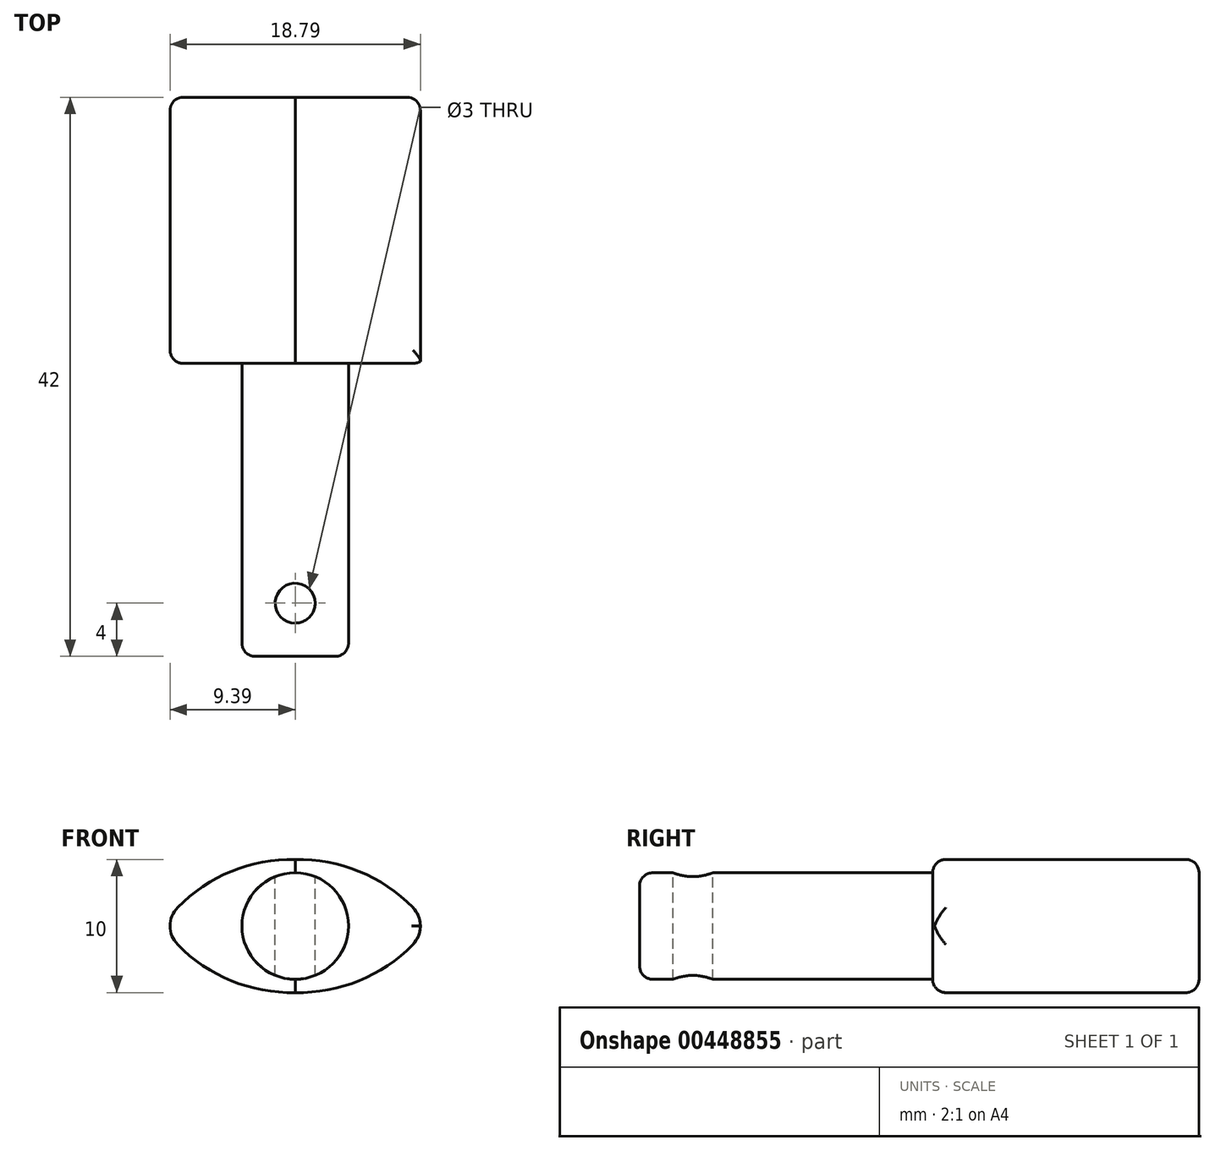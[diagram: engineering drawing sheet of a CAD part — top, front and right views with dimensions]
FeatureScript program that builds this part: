
annotation { "Feature Type Name" : "Feature", "Feature Type Description" : "" }
export const myFeature = defineFeature(function(context is Context, id is Id, definition is map)
    precondition{}
    {
        {
            var Q0;
            Q0=qCreatedBy(makeId("Front.planeOp"),FACE);
            var sketch = newSketch(context, id + "F0", { "sketchPlane" : qUnion([Q0])});
            skPoint(sketch, "E0", {"position": v(-10, -0.04) * mm});
            skPoint(sketch, "E1", {"position": v(0, 4.96) * mm});
            skPoint(sketch, "E2", {"position": v(0, -5.04) * mm});
            skPoint(sketch, "E3", {"position": v(10, -0.04) * mm});
            skArc(sketch, "E4", {"start": v(0, 4.96) * mm, "mid": v(-4.78, 4.07) * mm, "end": v(-8.82, 1.36) * mm});
            skArc(sketch, "E5", {"start": v(-8.82, -1.44) * mm, "mid": v(-4.78, -4.16) * mm, "end": v(0, -5.04) * mm});
            skArc(sketch, "E6", {"start": v(8.82, 1.36) * mm, "mid": v(4.79, 4.07) * mm, "end": v(0, 4.96) * mm});
            skArc(sketch, "E7", {"start": v(0, -5.04) * mm, "mid": v(4.79, -4.16) * mm, "end": v(8.82, -1.44) * mm});
            skArc(sketch, "E8.filletArc", {"start": v(-8.82, 1.36) * mm, "mid": v(-9.4, -0.04) * mm, "end": v(-8.82, -1.44) * mm});
            skArc(sketch, "E9.filletArc", {"start": v(8.82, -1.44) * mm, "mid": v(9.4, -0.04) * mm, "end": v(8.82, 1.36) * mm});
            skLineSegment(sketch, "E10", {"start": v(0, -0.04) * mm, "end": v(0, 4.96) * mm, "construction": true});
            skLineSegment(sketch, "E11", {"start": v(-10, -0.04) * mm, "end": v(0, -0.04) * mm, "construction": true});
            skLineSegment(sketch, "E12.trimOffspring", {"start": v(9.4, -0.04) * mm, "end": v(10, -0.04) * mm, "construction": true});
            skSolve(sketch);
        }
        {
            var Q0;
            Q0=makeQuery(id+"F0.imprint","IMPRINT",FACE,{"disambiguationData":[TD([[makeQuery(id+"F0.imprint","IMPRINT",EDGE,{"derivedFrom":sQuery(id+"F0.wireOp",EDGE,"E4")}),1.0]])]});
            extrude(context, id + "F1", {"entities" : qUnion([Q0]), "depth" : 20 * mm});
        }
        {
            var Q0;
            Q0=makeQuery(id+"F1.opExtrude","CAP_FACE",FACE,{"disambiguationData":[OSD([sQuery(id+"F0.wireOp",EDGE,"E4"),sQuery(id+"F0.wireOp",EDGE,"E5"),sQuery(id+"F0.wireOp",EDGE,"E6"),sQuery(id+"F0.wireOp",EDGE,"E7"),sQuery(id+"F0.wireOp",EDGE,"E8.filletArc"),sQuery(id+"F0.wireOp",EDGE,"E9.filletArc")])],"isStart":false});
            var sketch = newSketch(context, id + "F2", { "sketchPlane" : qUnion([Q0])});
            skCircle(sketch, "E13", {"center": v(0, -0.04) * mm, "radius": 4 * mm});
            skPoint(sketch, "E13.centerSnap0", {"position": v(-5.4, -0.04) * mm});
            skSolve(sketch);
        }
        {
            var Q0;
            Q0=makeQuery(id+"F2.imprint","IMPRINT",FACE,{"disambiguationData":[TD([[makeQuery(id+"F2.imprint","IMPRINT",EDGE,{"derivedFrom":sQuery(id+"F2.wireOp",EDGE,"E13")}),1.0]])]});
            extrude(context, id + "F3", {"entities" : qUnion([Q0]), "operationType" : NewBodyOperationType.ADD, "depth" : 22 * mm});
        }
        {
            var Q0;
            Q0=qCreatedBy(makeId("Top.planeOp"),FACE);
            var sketch = newSketch(context, id + "F4", { "sketchPlane" : qUnion([Q0])});
            skCircle(sketch, "E14", {"center": v(0, -38) * mm, "radius": 1.5 * mm});
            skSolve(sketch);
        }
        {
            var Q0;
            Q0 = qSketchRegion(id + "F4", true);
            extrude(context, id + "F5", {"entities" : qUnion([Q0]), "operationType" : NewBodyOperationType.REMOVE, "endBound" : BoundingType.SYMMETRIC, "oppositeDirection" : true, "depth" : 10 * mm});
        }
        {
            var Q0;
            Q0=makeQuery(id+"F1.opExtrude","CAP_EDGE",EDGE,{"disambiguationData":[OSD([sQuery(id+"F0.wireOp",EDGE,"E5")])],"isStart":false});
            var Q1;
            Q1=makeQuery(id+"F1.opExtrude","CAP_EDGE",EDGE,{"disambiguationData":[OSD([sQuery(id+"F0.wireOp",EDGE,"E5")])],"isStart":true});
            var Q2;
            Q2=makeQuery(id+"F3.opExtrude","CAP_EDGE",EDGE,{"disambiguationData":[OSD([sQuery(id+"F2.wireOp",EDGE,"E13")])],"isStart":false});
            fillet(context, id + "F6", {"entities" : qUnion([Q0, Q1, Q2]), "radius" : 1 * mm, "tangentPropagation" : true, "allowEdgeOverflow" : false});
        }
    });
